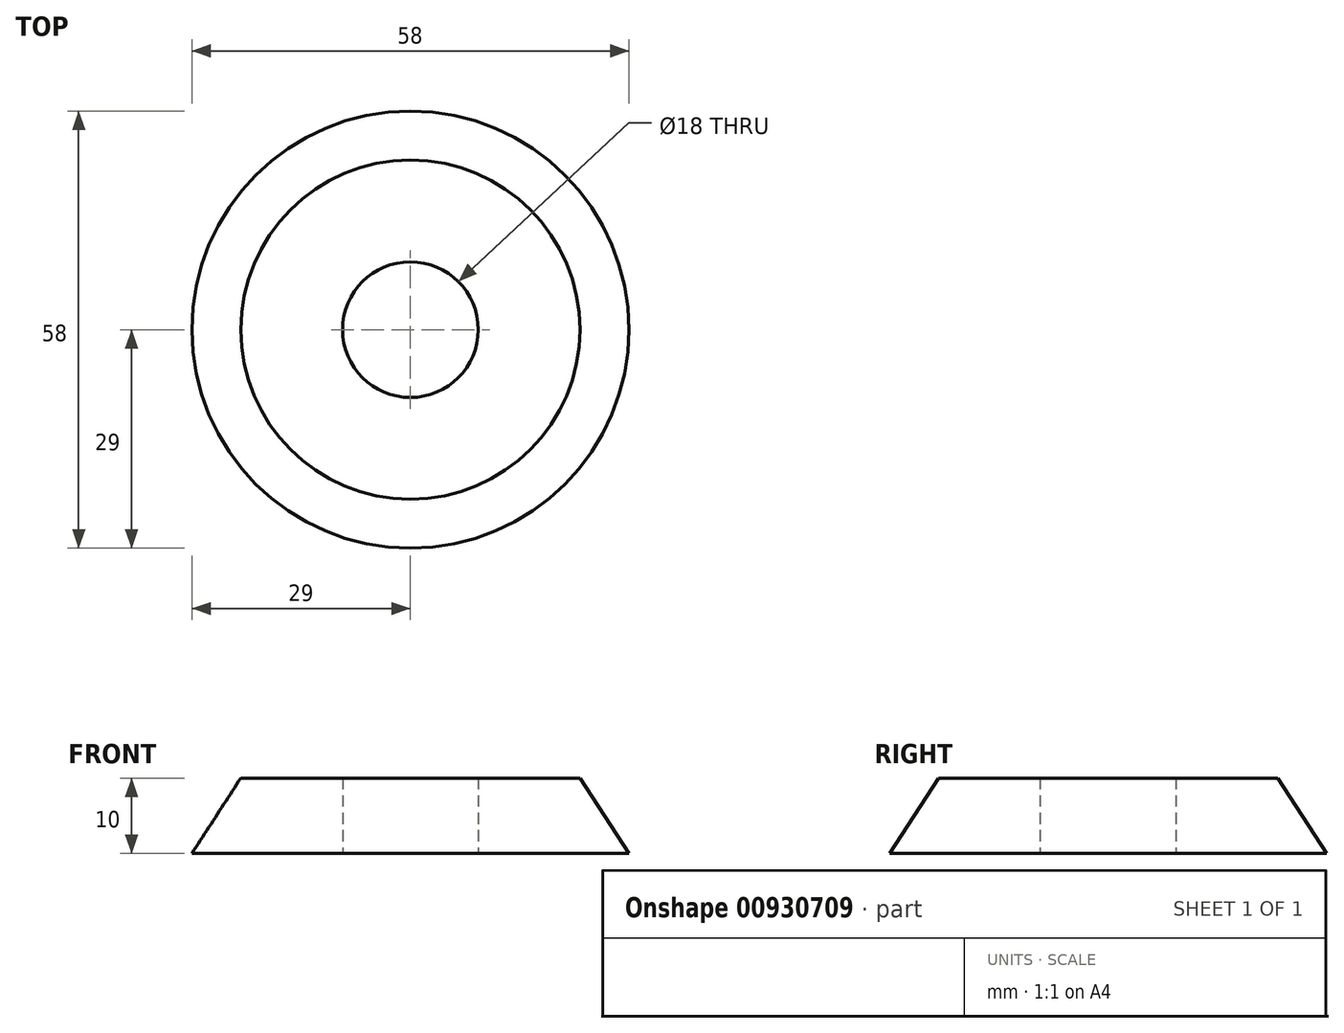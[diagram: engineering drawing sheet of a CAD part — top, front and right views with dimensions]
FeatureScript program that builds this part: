
annotation { "Feature Type Name" : "Feature", "Feature Type Description" : "" }
export const myFeature = defineFeature(function(context is Context, id is Id, definition is map)
    precondition{}
    {
        {
            var Q0;
            Q0=qCreatedBy(makeId("Top.planeOp"),FACE);
            var sketch = newSketch(context, id + "F0", { "sketchPlane" : qUnion([Q0])});
            skCircle(sketch, "E0", {"center": v(0, 0) * mm, "radius": 29 * mm});
            skCircle(sketch, "E1", {"center": v(0, 0) * mm, "radius": 9 * mm});
            skSolve(sketch);
        }
        {
            var Q0;
            Q0=makeQuery(id+"F0.imprint","IMPRINT",FACE,{"disambiguationData":[TD([[makeQuery(id+"F0.imprint","IMPRINT",EDGE,{"derivedFrom":sQuery(id+"F0.wireOp",EDGE,"E0")}),1.0]])]});
            cPlane(context, id + "F1", {"entities" : qUnion([Q0]), "cplaneType" : CPlaneType.OFFSET, "offset" : 10 * mm, "width" : 150 * mm, "height" : 150 * mm});
        }
        {
            var Q0;
            Q0=qCreatedBy(id+"F1.planeOp",FACE);
            var sketch = newSketch(context, id + "F2", { "sketchPlane" : qUnion([Q0])});
            skCircle(sketch, "E2.0", {"center": v(0, 0) * mm, "radius": 9 * mm});
            skCircle(sketch, "E3", {"center": v(0, 0) * mm, "radius": 22.5 * mm});
            skSolve(sketch);
        }
        {
            var Q0;
            Q0=qCreatedBy(makeId("Front.planeOp"),FACE);
            var sketch = newSketch(context, id + "F3", { "sketchPlane" : qUnion([Q0])});
            skLineSegment(sketch, "E4.0", {"start": v(-22.5, 10) * mm, "end": v(22.5, 10) * mm});
            skLineSegment(sketch, "E5.0", {"start": v(-29, 0) * mm, "end": v(29, 0) * mm});
            skLineSegment(sketch, "E6.0", {"start": v(-9, 0) * mm, "end": v(9, 0) * mm});
            skLineSegment(sketch, "E7.0", {"start": v(-9, 10) * mm, "end": v(9, 10) * mm});
            skLineSegment(sketch, "E8", {"start": v(-29, 0) * mm, "end": v(-22.5, 10) * mm});
            skLineSegment(sketch, "E9", {"start": v(-9, 10) * mm, "end": v(-9, 0) * mm});
            skLineSegment(sketch, "E10", {"start": v(0, -2.17) * mm, "end": v(0, 38.96) * mm});
            skSolve(sketch);
        }
        {
            var Q0;
            {var subQ0=sQuery(id+"F3.wireOp",EDGE,"E8");Q0=makeQuery(id+"F3.imprint","IMPRINT",FACE,{"disambiguationData":[TD([[makeQuery(id+"F3.imprint","IMPRINT",EDGE,{"derivedFrom":subQ0}),-1.0]])]});}
            var Q1;
            Q1=sQuery(id+"F3.wireOp",EDGE,"E10");
            revolve(context, id + "F4", {"surfaceOperationType" : NewSurfaceOperationType.NEW, "entities" : qUnion([Q0]), "axis" : qUnion([Q1]), "revolveType" : RevolveType.FULL});
        }
    });
